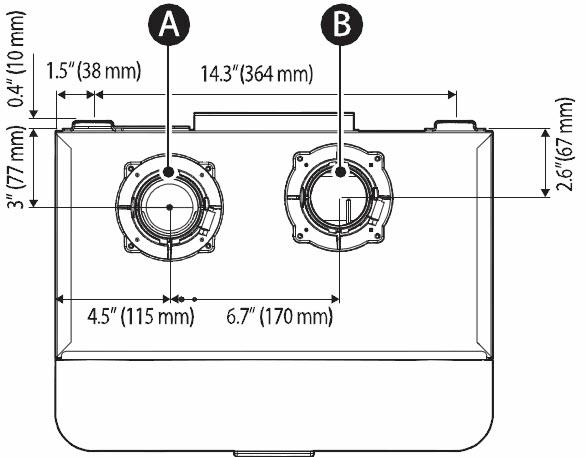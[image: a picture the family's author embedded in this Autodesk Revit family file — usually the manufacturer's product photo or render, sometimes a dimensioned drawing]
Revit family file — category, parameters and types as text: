
# Revit family: Water_Heater-Racks-Navien-NPE-16_Unit_Front---
name_source: partatom
category: Mechanical Equipment
revit_build: Autodesk Revit 2016 (Build: 20150220_1215(x64)
units: mm (PartAtom-declared; Revit-internal decimal feet)

## family parameters
Cut with Voids When Loaded = No
Host = Face
OmniClass Number = 23.65.35.11
OmniClass Title = Supply Water Heaters
Part Type = Normal
Room Calculation Point = No
Round Connector Dimension = Use Diameter
Shared = No

## types (4) — shared parameters
2" Exhaust/Intake = Yes
3" Exhaust/Intake = No
Apparent Load = 0 VA
Assembly Code = D3010500
Certifications = Energy Star | AHRI | CSA | CSA | NFS
Cold Water Inlet = 1"
Configuration = NPE_F16_4F4F_4F4F
Default Elevation = 48 "
Depth = 23.8 "
Description = 16 Unit Front
Exhaust = 2"
Finish = Metal - Navien - White
Flow Rate = 1 GPM
Flow Rate Note = 35°F (19°C) temp rise: 11.2 GPM (42 L/m) | 45°F (25°C) temp rise: 8.7 GPM (33 L/m) | 67°F (36°C) temp rise: NPE-240A: 5.6 GPM(21 L/m), NPE-240S: 5.7 GPM(22 L/m)
Frequency = 60 Hz
Gas Inlet = 1"
Heating Capacity = 120000.0 Btu/h
Heating Capacity Note = 19,900–199,900 (BTU/H)
Height = 65.5 "
Hot Water Outlet = 1"
Ignition = Electronic ignition
Installation Type = Indoor
Intake = 2"
Keynote = 22 33 00.A1
Manifold(s) = (4) 30019043A
Manufacturer = Navien, Inc.
Manufacturer Fax Number = (949) 420-0430
Natural Gas Manifold Pressure = -0.05" WC to -0.58" WC
Natural Gas Supply Pressure = 3.5"–10.5" WC
Number of Poles = 1
Phase = 1
Power Factor = 1
Product Documentation Link = https://www.navieninc.com
Product Name = NPE Series Tankless Water Heaters w/ Racks
Product Page URL = https://www.navieninc.com
Propane Gas Manifold Pressure = -0.10" WC to -0.78" WC
Propane Gas Supply Pressure = 8"–13" WC
Rack(s) = (2) GFFM-KDIZUS-003 + (14) GFFM-KDIZUS-004
Required Cascade Operation Accessory = (16) 30014367A (Common Vent Damper & Cascade Communication Cable) or (1) GXXX000546 (Individual Vent Cascade Communication Cable)
URL = https://www.navieninc.com
Venting = Exhaust: 2" PVC, CPVC, PP, SS / 2" special gas vent type BH (Class II, A/B/C) | Intake: 2" PVC, CPVC, PP, SS / 2" special gas vent type BH (Class II, A/B/C) | Vent clearances: 0" to combustibles
Venting Type = Forced draft direct vent
Version = 2016 - v1.0.a
Voltage = 120 V
Water Pressure = 15–150 PSI
Wi-Fi Ready = NaviLink Wi-Fi Control: PBCM-AS-001
Width = 342.3 "

## per-type parameters (varying)
| type | Constraints | Model | Natural Gas | Propane Gas | Recirculation Inlet | Recirculation Inlet Visibility | Tankless Water Heaters | Weight |
| Natural Gas - Recirculating System - NPE-240A(Advanced)-NG | 6 | (16) NPE-240A-NG | Yes | No | 0" | Yes | (16) NPE-240A-NG | 82.00 lbf |
| Natural Gas - NPE-240S(Standard)-NG | 7 | (16) NPE-240S-NG | Yes | No | 1" | No | (16) NPE-240S-NG | 75.00 lbf |
| Propane Gas - Recirculating System - NPE-240A(Advanced)-LPG | 6 | (16) NPE-240A-LPG | No | Yes | 0" | Yes | (16) NPE-240A-LPG | 82.00 lbf |
| Propane Gas - NPE-240S(Standard)-LPG | 7 | (16) NPE-240S-LPG | No | Yes | 1" | No | (16) NPE-240S-LPG | 75.00 lbf |

## geometry (parser evidence)
native form markers: Sweep x16
no freeform markers — native parametric forms only
